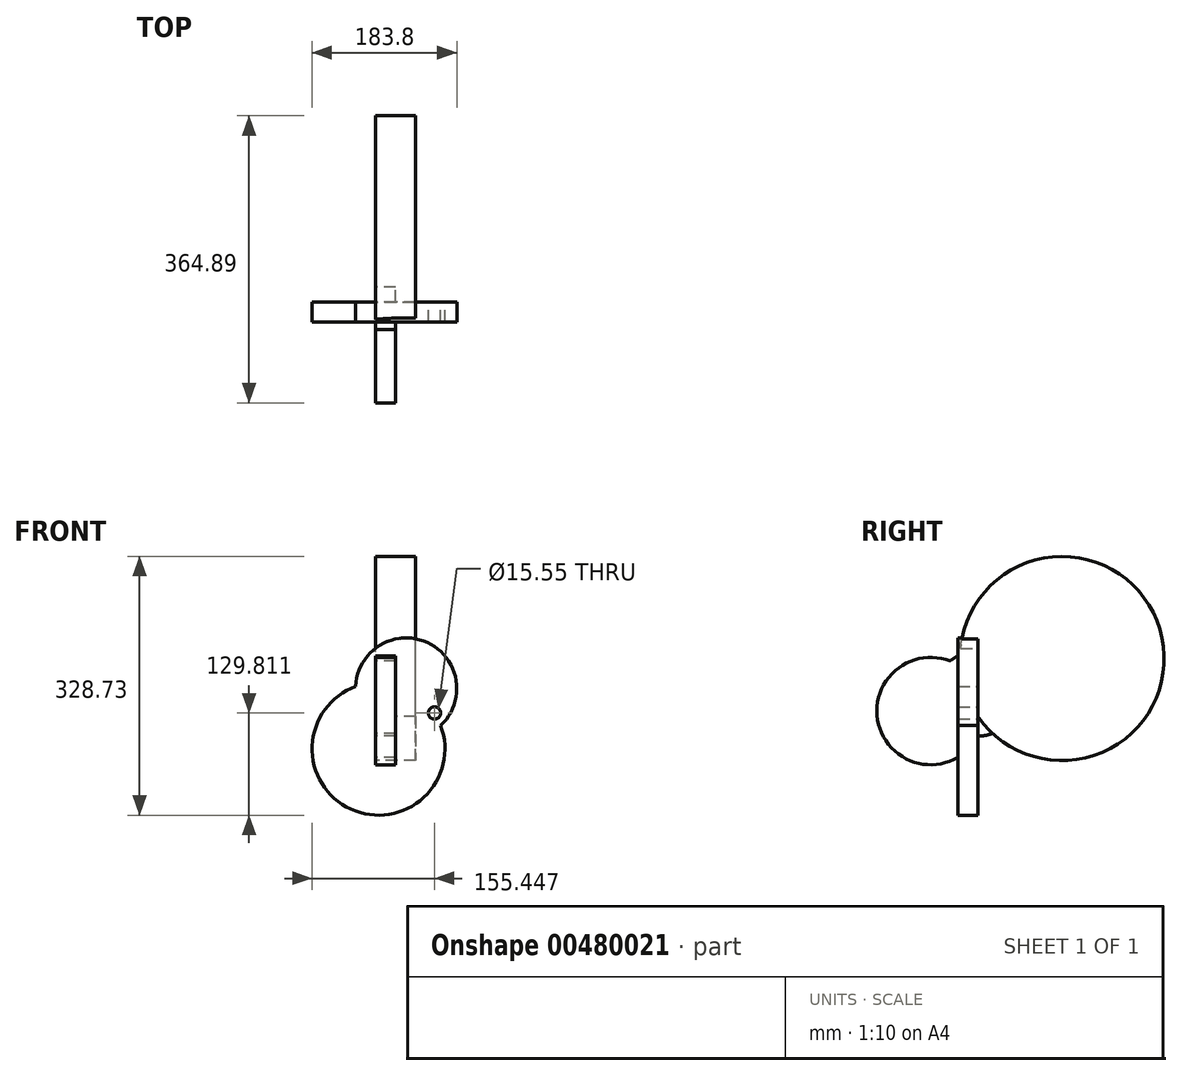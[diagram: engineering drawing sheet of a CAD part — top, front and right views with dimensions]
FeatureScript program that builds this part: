
annotation { "Feature Type Name" : "Feature", "Feature Type Description" : "" }
export const myFeature = defineFeature(function(context is Context, id is Id, definition is map)
    precondition{}
    {
        {
            var Q0;
            Q0=qCreatedBy(makeId("Right.planeOp"),FACE);
            var sketch = newSketch(context, id + "F0", { "sketchPlane" : qUnion([Q0])});
            skCircle(sketch, "E0", {"center": v(-0.62, 62.2) * mm, "radius": 54.03 * mm});
            skPoint(sketch, "E0.first.point", {"position": v(-46.07, 33) * mm});
            skPoint(sketch, "E0.second.point", {"position": v(-51.18, 43.16) * mm});
            skPoint(sketch, "E0.third.point", {"position": v(53.41, 61.7) * mm});
            skCircle(sketch, "E1", {"center": v(-60.26, 40.1) * mm, "radius": 68.2 * mm});
            skPoint(sketch, "E1.first.point", {"position": v(0, 8.18) * mm});
            skPoint(sketch, "E1.second.point", {"position": v(-35.37, 103.58) * mm});
            skPoint(sketch, "E1.third.point", {"position": v(-0.62, 73.14) * mm});
            skSolve(sketch);
        }
        {
            var Q0;
            Q0=qCreatedBy(makeId("Front.planeOp"),FACE);
            var sketch = newSketch(context, id + "F1", { "sketchPlane" : qUnion([Q0])});
            skArc(sketch, "E2", {"start": v(74.7, 37.57) * mm, "mid": v(41.45, 11.9) * mm, "end": v(0, 18.73) * mm});
            skArc(sketch, "E3", {"start": v(28.57, 62.97) * mm, "mid": v(30.45, 61.7) * mm, "end": v(32.27, 60.35) * mm});
            skArc(sketch, "E4", {"start": v(28.57, 62.97) * mm, "mid": v(28.04, 61.98) * mm, "end": v(27.52, 60.97) * mm});
            skArc(sketch, "E5", {"start": v(-16.09, 102) * mm, "mid": v(-15.72, 102.52) * mm, "end": v(-15.35, 103.03) * mm});
            skArc(sketch, "E6", {"start": v(0, 60.97) * mm, "mid": v(7.2, 63.06) * mm, "end": v(12.18, 68.68) * mm});
            skArc(sketch, "E7", {"start": v(0, 0) * mm, "mid": v(1.7, -3.99) * mm, "end": v(3.63, -7.87) * mm});
            skCircle(sketch, "E8", {"center": v(74.7, 37.57) * mm, "radius": 7.78 * mm});
            skCircle(sketch, "E9", {"center": v(3.63, -7.87) * mm, "radius": 84.37 * mm});
            skCircle(sketch, "E10", {"center": v(38.85, 68.79) * mm, "radius": 64.2 * mm});
            skSolve(sketch);
        }
        {
            var Q0;
            Q0 = qSketchRegion(id + "F1", true);
            extrude(context, id + "F2", {"entities" : qUnion([Q0]), "depth" : 25.4 * mm});
        }
        {
            var Q0;
            {var subQ0=sQuery(id+"F0.wireOp",EDGE,"E1");var subQ1=sQuery(id+"F0.wireOp",EDGE,"E0");var subQ2=makeQuery(id+"F0.imprint","INTERSECT",VERTEX,{"disambiguationData":[OD(0.0)],"derivedFrom":[subQ1,subQ0]});Q0=makeQuery(id+"F0.imprint","IMPRINT",FACE,{"disambiguationData":[TD([[makeQuery(id+"F0.imprint","IMPRINT",EDGE,{"disambiguationData":[TD([[subQ2,1.0]])],"derivedFrom":subQ1}),-1.0]])]});}
            var sketch = newSketch(context, id + "F3", { "sketchPlane" : qUnion([Q0])});
            skCircle(sketch, "E11", {"center": v(106.74, 106.8) * mm, "radius": 129.7 * mm});
            skSolve(sketch);
        }
        {
            var Q0;
            Q0 = qSketchRegion(id + "F3", true);
            extrude(context, id + "F4", {"entities" : qUnion([Q0]), "operationType" : NewBodyOperationType.ADD, "depth" : 25.4 * mm});
        }
        {
            var Q0;
            {var subQ0=sQuery(id+"F0.wireOp",EDGE,"E1");var subQ1=sQuery(id+"F0.wireOp",EDGE,"E0");var subQ2=makeQuery(id+"F0.imprint","INTERSECT",VERTEX,{"disambiguationData":[OD(0.0)],"derivedFrom":[subQ1,subQ0]});Q0=makeQuery(id+"F0.imprint","IMPRINT",FACE,{"disambiguationData":[TD([[makeQuery(id+"F0.imprint","IMPRINT",EDGE,{"disambiguationData":[TD([[subQ2,1.0]])],"derivedFrom":subQ1}),-1.0]])]});}
            var Q1;
            Q1 = qSketchRegion(id + "F0", true);
            var Q2;
            Q2=makeQuery(id+"F4.opExtrude","CAP_FACE",FACE,{"disambiguationData":[OSD([sQuery(id+"F3.wireOp",EDGE,"E11")])],"isStart":false});
            var Q3;
            {var subQ0=sQuery(id+"F0.wireOp",EDGE,"E1");var subQ1=sQuery(id+"F0.wireOp",EDGE,"E0");var subQ2=makeQuery(id+"F0.imprint","INTERSECT",VERTEX,{"disambiguationData":[OD(0.0)],"derivedFrom":[subQ1,subQ0]});Q3=makeQuery(id+"F0.imprint","IMPRINT",FACE,{"disambiguationData":[TD([[makeQuery(id+"F0.imprint","IMPRINT",EDGE,{"disambiguationData":[TD([[subQ2,1.0]])],"derivedFrom":subQ1}),1.0]])]});}
            extrude(context, id + "F5", {"entities" : qUnion([Q0, Q1, Q2, Q3]), "operationType" : NewBodyOperationType.ADD, "depth" : 25.4 * mm});
        }
    });
